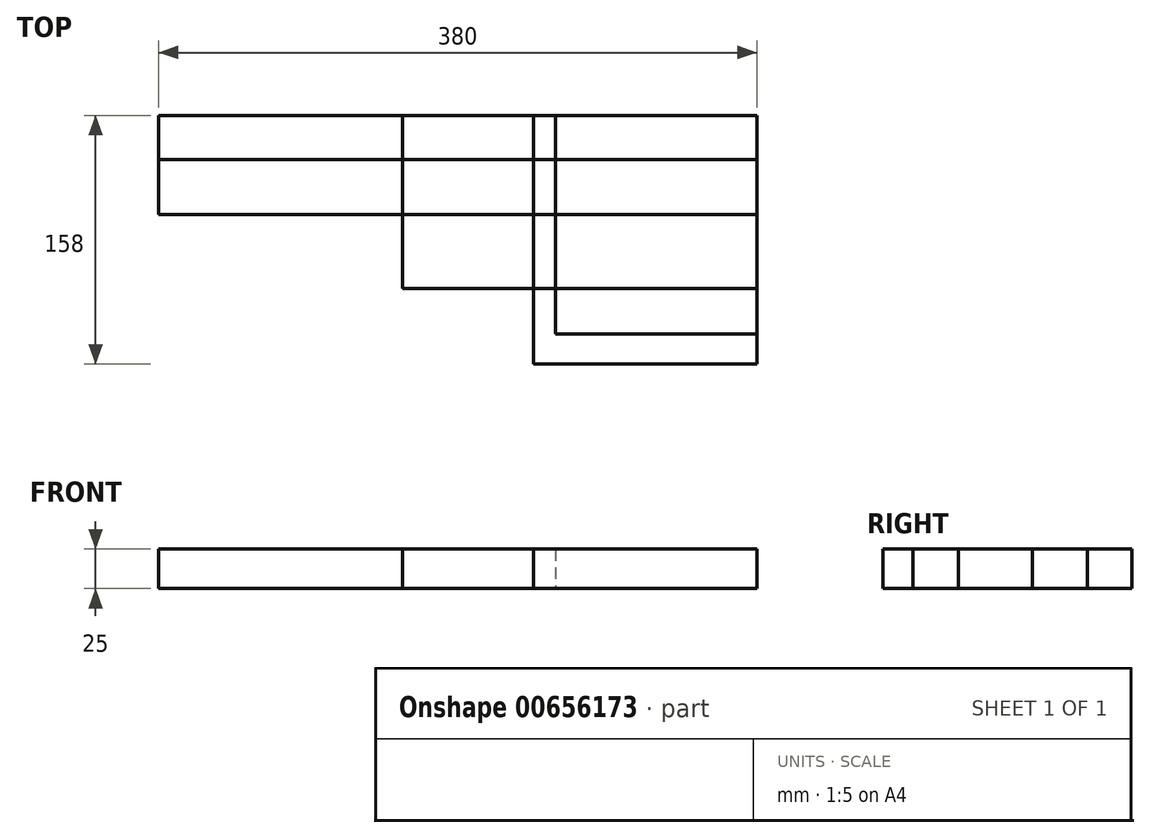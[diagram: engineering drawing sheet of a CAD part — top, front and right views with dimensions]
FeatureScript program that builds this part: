
annotation { "Feature Type Name" : "Feature", "Feature Type Description" : "" }
export const myFeature = defineFeature(function(context is Context, id is Id, definition is map)
    precondition{}
    {
        {
            var Q0;
            Q0=qCreatedBy(makeId("Top.planeOp"),FACE);
            var sketch = newSketch(context, id + "F0", { "sketchPlane" : qUnion([Q0])});
            skLineSegment(sketch, "E0.bottom", {"start": v(0, 0) * mm, "end": v(-225, 0) * mm});
            skLineSegment(sketch, "E0.top", {"start": v(0, -110) * mm, "end": v(-225, -110) * mm});
            skLineSegment(sketch, "E0.left", {"start": v(0, 0) * mm, "end": v(0, -110) * mm});
            skLineSegment(sketch, "E0.right", {"start": v(-225, 0) * mm, "end": v(-225, -110) * mm});
            skSolve(sketch);
        }
        {
            var Q0;
            Q0 = qSketchRegion(id + "F0", true);
            extrude(context, id + "F1", {"entities" : qUnion([Q0]), "depth" : 25 * mm, "offsetDistance" : 25 * mm});
        }
        {
            var Q0;
            Q0=qCreatedBy(makeId("Top.planeOp"),FACE);
            var sketch = newSketch(context, id + "F2", { "sketchPlane" : qUnion([Q0])});
            skLineSegment(sketch, "E1.bottom", {"start": v(0, 0) * mm, "end": v(-142, 0) * mm});
            skLineSegment(sketch, "E1.top", {"start": v(0, -158) * mm, "end": v(-142, -158) * mm});
            skLineSegment(sketch, "E1.left", {"start": v(0, 0) * mm, "end": v(0, -158) * mm});
            skLineSegment(sketch, "E1.right", {"start": v(-142, 0) * mm, "end": v(-142, -158) * mm});
            skSolve(sketch);
        }
        {
            var Q0;
            Q0 = qSketchRegion(id + "F2", true);
            extrude(context, id + "F3", {"entities" : qUnion([Q0]), "depth" : 25 * mm, "offsetDistance" : 25 * mm});
        }
        {
            var Q0;
            Q0=qCreatedBy(makeId("Top.planeOp"),FACE);
            var sketch = newSketch(context, id + "F4", { "sketchPlane" : qUnion([Q0])});
            skLineSegment(sketch, "E2.bottom", {"start": v(0, 0) * mm, "end": v(-128, 0) * mm});
            skLineSegment(sketch, "E2.top", {"start": v(0, -139) * mm, "end": v(-128, -139) * mm});
            skLineSegment(sketch, "E2.left", {"start": v(0, 0) * mm, "end": v(0, -139) * mm});
            skLineSegment(sketch, "E2.right", {"start": v(-128, 0) * mm, "end": v(-128, -139) * mm});
            skSolve(sketch);
        }
        {
            var Q0;
            Q0 = qSketchRegion(id + "F4", true);
            extrude(context, id + "F5", {"entities" : qUnion([Q0]), "depth" : 25 * mm, "offsetDistance" : 25 * mm});
        }
        {
            var Q0;
            Q0=qCreatedBy(makeId("Top.planeOp"),FACE);
            var sketch = newSketch(context, id + "F6", { "sketchPlane" : qUnion([Q0])});
            skLineSegment(sketch, "E3.bottom", {"start": v(0, 0) * mm, "end": v(-380, 0) * mm});
            skLineSegment(sketch, "E3.top", {"start": v(0, -63) * mm, "end": v(-380, -63) * mm});
            skLineSegment(sketch, "E3.left", {"start": v(0, 0) * mm, "end": v(0, -63) * mm});
            skLineSegment(sketch, "E3.right", {"start": v(-380, 0) * mm, "end": v(-380, -63) * mm});
            skSolve(sketch);
        }
        {
            var Q0;
            Q0 = qSketchRegion(id + "F6", true);
            extrude(context, id + "F7", {"entities" : qUnion([Q0]), "depth" : 25 * mm, "offsetDistance" : 25 * mm});
        }
        {
            var Q0;
            Q0=qCreatedBy(makeId("Top.planeOp"),FACE);
            var sketch = newSketch(context, id + "F8", { "sketchPlane" : qUnion([Q0])});
            skLineSegment(sketch, "E4.bottom", {"start": v(0, 0) * mm, "end": v(-380, 0) * mm});
            skLineSegment(sketch, "E4.top", {"start": v(0, -28) * mm, "end": v(-380, -28) * mm});
            skLineSegment(sketch, "E4.left", {"start": v(0, 0) * mm, "end": v(0, -28) * mm});
            skLineSegment(sketch, "E4.right", {"start": v(-380, 0) * mm, "end": v(-380, -28) * mm});
            skSolve(sketch);
        }
        {
            var Q0;
            Q0 = qSketchRegion(id + "F8", true);
            extrude(context, id + "F9", {"entities" : qUnion([Q0]), "depth" : 25 * mm, "offsetDistance" : 25 * mm});
        }
    });
